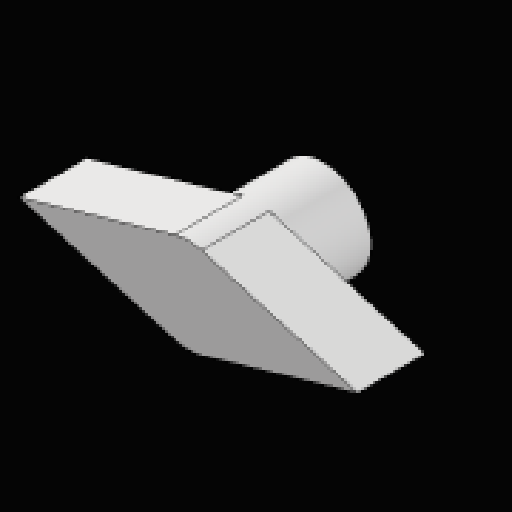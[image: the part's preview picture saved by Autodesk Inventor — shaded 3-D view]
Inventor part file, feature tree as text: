
AUTODESK INVENTOR PART (.ipt)
format: ipt  version: 2023.2 (Build 272271030, 271C)  size: 96,256 bytes
history: native  units: mm
features: extrude x2, sketch x2, projected_geometry x1
ambient origin geometry x8: Origin, YZ Plane, XZ Plane, XY Plane, X Axis, Y Axis, Z Axis, Center Point
bodies: Solid1 (feature_tree)
feature tree (5):
  extrude  "Extrusion1"  Depth=6.0mm TaperAngle=0.0deg
  extrude  "Extrusion2"  Depth=5.0mm TaperAngle=0.0deg
  sketch  "Sketch1"  dims[d0=7.0mm d1=6.0mm d2=0.0mm]
  sketch  "Sketch2"  dims[d3=30.0mm d4=5.0mm d5=0.0mm d6=0.5mm d7=0.872665mm d8=0.5mm d9=0.872665mm]
  projected_geometry  "Projected Loop1"
